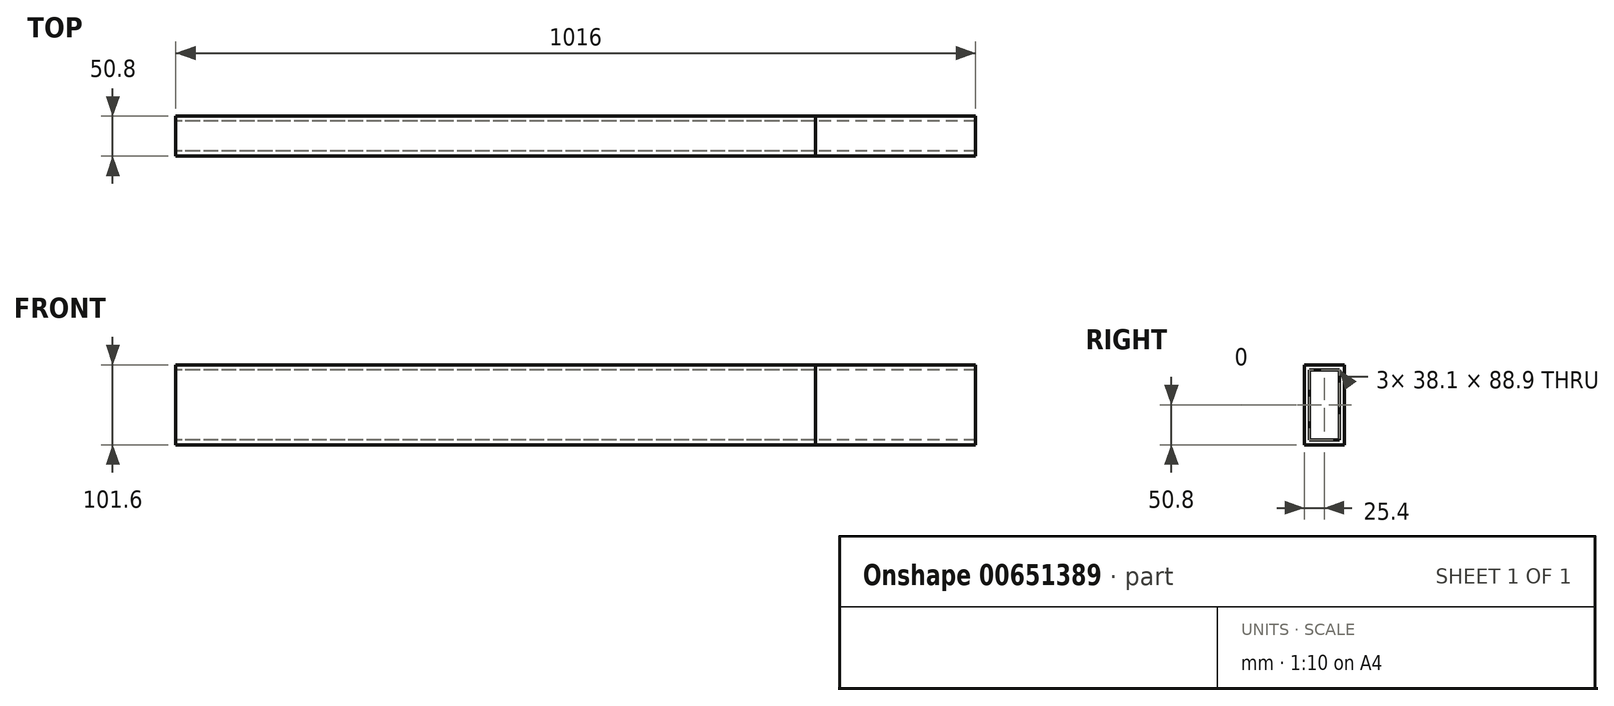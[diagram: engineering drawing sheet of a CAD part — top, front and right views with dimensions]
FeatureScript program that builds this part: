
annotation { "Feature Type Name" : "Feature", "Feature Type Description" : "" }
export const myFeature = defineFeature(function(context is Context, id is Id, definition is map)
    precondition{}
    {
        {
            var Q0;
            Q0=qCreatedBy(makeId("Right.planeOp"),FACE);
            var sketch = newSketch(context, id + "F0", { "sketchPlane" : qUnion([Q0])});
            skLineSegment(sketch, "E0.bottom", {"start": v(0, 0) * mm, "end": v(-50.8, 0) * mm});
            skLineSegment(sketch, "E0.top", {"start": v(0, 101.6) * mm, "end": v(-50.8, 101.6) * mm});
            skLineSegment(sketch, "E0.left", {"start": v(0, 0) * mm, "end": v(0, 101.6) * mm});
            skLineSegment(sketch, "E0.right", {"start": v(-50.8, 0) * mm, "end": v(-50.8, 101.6) * mm});
            skLineSegment(sketch, "E1.bottom", {"start": v(-6.35, 6.35) * mm, "end": v(-44.45, 6.35) * mm});
            skLineSegment(sketch, "E1.top", {"start": v(-6.35, 95.25) * mm, "end": v(-44.45, 95.25) * mm});
            skLineSegment(sketch, "E1.left", {"start": v(-6.35, 6.35) * mm, "end": v(-6.35, 95.25) * mm});
            skLineSegment(sketch, "E1.right", {"start": v(-44.45, 6.35) * mm, "end": v(-44.45, 95.25) * mm});
            skSolve(sketch);
        }
        {
            var Q0;
            Q0=makeQuery(id+"F0.imprint","IMPRINT",FACE,{"disambiguationData":[TD([[makeQuery(id+"F0.imprint","IMPRINT",EDGE,{"derivedFrom":sQuery(id+"F0.wireOp",EDGE,"E0.bottom")}),-1.0]])]});
            extrude(context, id + "F1", {"entities" : qUnion([Q0]), "depth" : 812.8 * mm, "offsetDistance" : 25.4 * mm});
        }
        {
            var Q0;
            Q0 = qSketchRegion(id + "F0", true);
            extrude(context, id + "F2", {"entities" : qUnion([Q0]), "depth" : 1016 * mm, "offsetDistance" : 25.4 * mm});
        }
        {
            var Q0;
            Q0 = qSketchRegion(id + "F0", true);
            extrude(context, id + "F3", {"entities" : qUnion([Q0]), "depth" : 1016 * mm, "offsetDistance" : 25.4 * mm});
        }
    });
